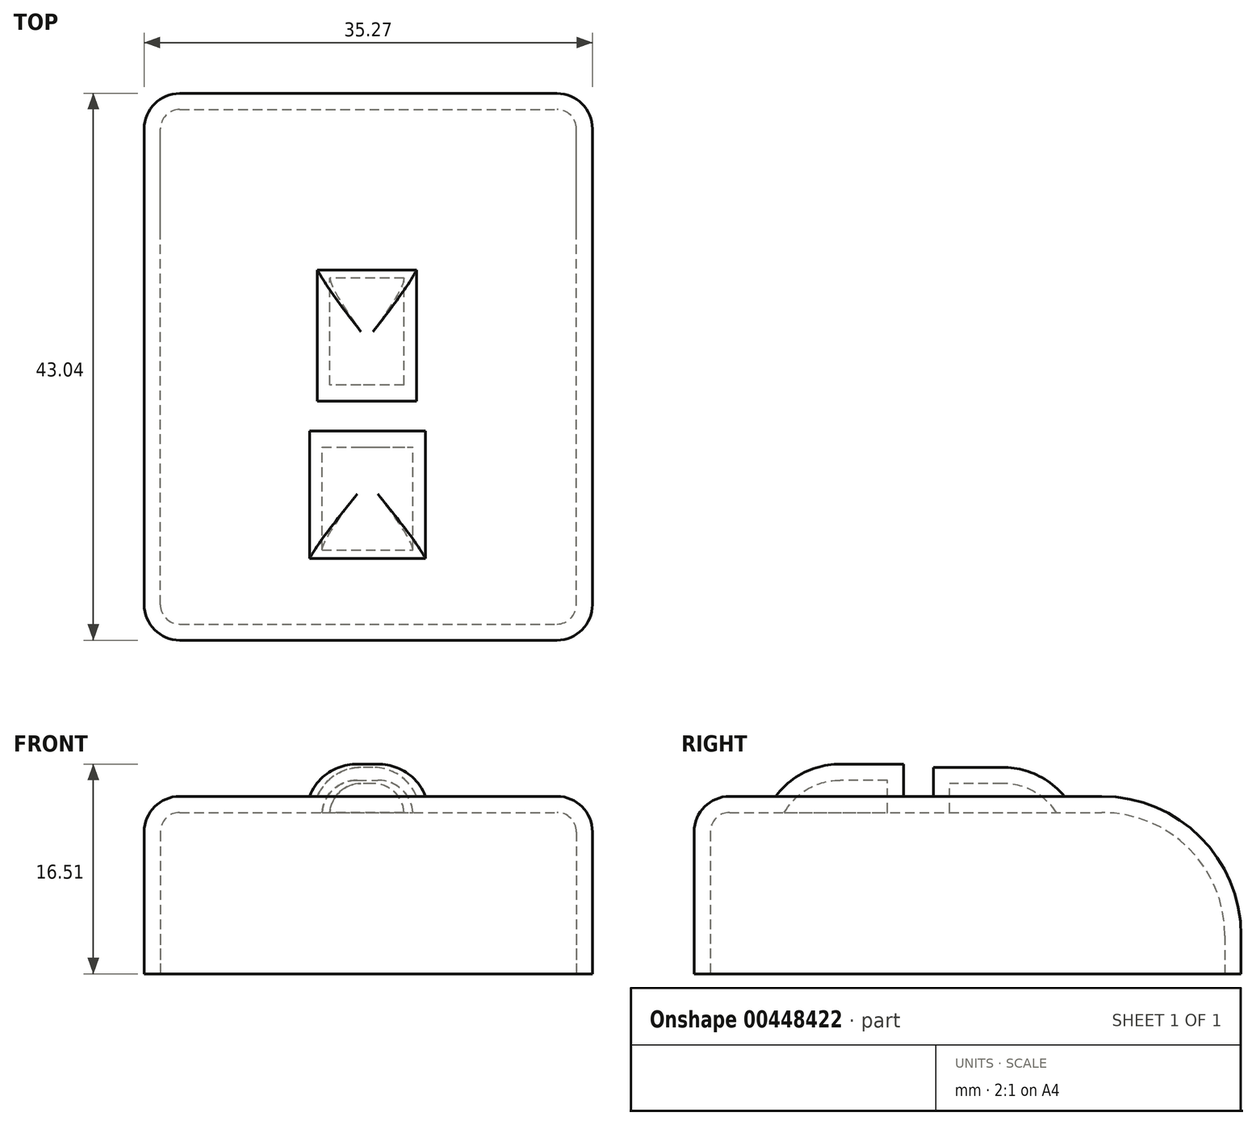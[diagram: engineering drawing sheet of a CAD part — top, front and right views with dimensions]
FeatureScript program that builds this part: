
annotation { "Feature Type Name" : "Feature", "Feature Type Description" : "" }
export const myFeature = defineFeature(function(context is Context, id is Id, definition is map)
    precondition{}
    {
        {
            var Q0;
            Q0=qCreatedBy(makeId("Top.planeOp"),FACE);
            var sketch = newSketch(context, id + "F0", { "sketchPlane" : qUnion([Q0])});
            skLineSegment(sketch, "E0.bottom", {"start": v(0, 0) * mm, "end": v(32.73, 0) * mm});
            skLineSegment(sketch, "E0.top", {"start": v(0, 40.5) * mm, "end": v(32.73, 40.5) * mm});
            skLineSegment(sketch, "E0.left", {"start": v(0, 0) * mm, "end": v(0, 40.5) * mm});
            skLineSegment(sketch, "E0.right", {"start": v(32.73, 0) * mm, "end": v(32.73, 40.5) * mm});
            skSolve(sketch);
        }
        {
            var Q0;
            Q0 = qSketchRegion(id + "F0", true);
            extrude(context, id + "F1", {"entities" : qUnion([Q0]), "depth" : 12.7 * mm});
        }
        {
            var Q0;
            Q0=makeQuery(id+"F1.opExtrude","CAP_EDGE",EDGE,{"disambiguationData":[OSD([sQuery(id+"F0.wireOp",EDGE,"E0.left")])],"isStart":false});
            var Q1;
            Q1=makeQuery(id+"F1.opExtrude","SWEPT_EDGE",EDGE,{"disambiguationData":[OSD([sQuery(id+"F0.wireOp",EDGE,"E0.bottom"),sQuery(id+"F0.wireOp",EDGE,"E0.left")])]});
            var Q2;
            Q2=makeQuery(id+"F1.opExtrude","SWEPT_EDGE",EDGE,{"disambiguationData":[OSD([sQuery(id+"F0.wireOp",EDGE,"E0.top"),sQuery(id+"F0.wireOp",EDGE,"E0.left")])]});
            var Q3;
            Q3=makeQuery(id+"F1.opExtrude","SWEPT_EDGE",EDGE,{"disambiguationData":[OSD([sQuery(id+"F0.wireOp",EDGE,"E0.bottom"),sQuery(id+"F0.wireOp",EDGE,"E0.right")])]});
            var Q4;
            Q4=makeQuery(id+"F1.opExtrude","CAP_EDGE",EDGE,{"disambiguationData":[OSD([sQuery(id+"F0.wireOp",EDGE,"E0.right")])],"isStart":false});
            var Q5;
            Q5=makeQuery(id+"F1.opExtrude","CAP_EDGE",EDGE,{"disambiguationData":[OSD([sQuery(id+"F0.wireOp",EDGE,"E0.bottom")])],"isStart":false});
            var Q6;
            Q6=makeQuery(id+"F1.opExtrude","SWEPT_EDGE",EDGE,{"disambiguationData":[OSD([sQuery(id+"F0.wireOp",EDGE,"E0.top"),sQuery(id+"F0.wireOp",EDGE,"E0.right")])]});
            fillet(context, id + "F2", {"entities" : qUnion([Q0, Q1, Q2, Q3, Q4, Q5, Q6]), "radius" : 1.52 * mm, "tangentPropagation" : true, "allowEdgeOverflow" : false});
        }
        {
            var Q0;
            Q0=makeQuery(id+"F1.opExtrude","CAP_EDGE",EDGE,{"disambiguationData":[OSD([sQuery(id+"F0.wireOp",EDGE,"E0.top")])],"isStart":false});
            fillet(context, id + "F3", {"entities" : qUnion([Q0]), "radius" : 9.7 * mm, "tangentPropagation" : true, "allowEdgeOverflow" : false});
        }
        {
            var Q0;
            Q0=makeQuery(id+"F1.opExtrude","CAP_FACE",FACE,{"disambiguationData":[OSD([sQuery(id+"F0.wireOp",EDGE,"E0.bottom"),sQuery(id+"F0.wireOp",EDGE,"E0.top"),sQuery(id+"F0.wireOp",EDGE,"E0.left"),sQuery(id+"F0.wireOp",EDGE,"E0.right")])],"isStart":false});
            var sketch = newSketch(context, id + "F4", { "sketchPlane" : qUnion([Q0])});
            skLineSegment(sketch, "E1.bottom", {"start": v(12.73, 5.83) * mm, "end": v(19.88, 5.83) * mm});
            skLineSegment(sketch, "E1.top", {"start": v(12.73, 13.93) * mm, "end": v(19.88, 13.93) * mm});
            skLineSegment(sketch, "E1.left", {"start": v(12.73, 5.83) * mm, "end": v(12.73, 13.93) * mm});
            skLineSegment(sketch, "E1.right", {"start": v(19.88, 5.83) * mm, "end": v(19.88, 13.93) * mm});
            skSolve(sketch);
        }
        {
            var Q0;
            Q0 = qSketchRegion(id + "F4", true);
            extrude(context, id + "F5", {"entities" : qUnion([Q0]), "operationType" : NewBodyOperationType.ADD, "depth" : 2.54 * mm});
        }
        {
            var Q0;
            Q0=makeQuery(id+"F5.opExtrude","CAP_EDGE",EDGE,{"disambiguationData":[OSD([sQuery(id+"F4.wireOp",EDGE,"E1.bottom")])],"isStart":false});
            fillet(context, id + "F6", {"entities" : qUnion([Q0]), "radius" : 5.08 * mm, "tangentPropagation" : true, "allowEdgeOverflow" : false});
        }
        {
            var Q0;
            Q0=makeQuery(id+"F5.opExtrude","CAP_EDGE",EDGE,{"disambiguationData":[OSD([sQuery(id+"F4.wireOp",EDGE,"E1.left")])],"isStart":false});
            var Q1;
            Q1=makeQuery(id+"F5.opExtrude","CAP_EDGE",EDGE,{"disambiguationData":[OSD([sQuery(id+"F4.wireOp",EDGE,"E1.right")])],"isStart":false});
            fillet(context, id + "F7", {"entities" : qUnion([Q0, Q1]), "radius" : 2.76 * mm, "tangentPropagation" : true, "allowEdgeOverflow" : false});
        }
        {
            var Q0;
            Q0=makeQuery(id+"F1.opExtrude","CAP_FACE",FACE,{"disambiguationData":[OSD([sQuery(id+"F0.wireOp",EDGE,"E0.bottom"),sQuery(id+"F0.wireOp",EDGE,"E0.top"),sQuery(id+"F0.wireOp",EDGE,"E0.left"),sQuery(id+"F0.wireOp",EDGE,"E0.right")])],"isStart":false});
            var sketch = newSketch(context, id + "F8", { "sketchPlane" : qUnion([Q0])});
            skLineSegment(sketch, "E2.bottom", {"start": v(19.18, 18.82) * mm, "end": v(13.35, 18.82) * mm});
            skLineSegment(sketch, "E2.top", {"start": v(19.18, 27.23) * mm, "end": v(13.35, 27.23) * mm});
            skLineSegment(sketch, "E2.left", {"start": v(19.18, 18.82) * mm, "end": v(19.18, 27.23) * mm});
            skLineSegment(sketch, "E2.right", {"start": v(13.35, 18.82) * mm, "end": v(13.35, 27.23) * mm});
            skSolve(sketch);
        }
        {
            var Q0;
            Q0 = qSketchRegion(id + "F8", true);
            extrude(context, id + "F9", {"entities" : qUnion([Q0]), "operationType" : NewBodyOperationType.ADD, "depth" : 2.3 * mm});
        }
        {
            var Q0;
            Q0=makeQuery(id+"F9.opExtrude","CAP_EDGE",EDGE,{"disambiguationData":[OSD([sQuery(id+"F8.wireOp",EDGE,"E2.top")])],"isStart":false});
            fillet(context, id + "F10", {"entities" : qUnion([Q0]), "radius" : 5.08 * mm, "tangentPropagation" : true, "allowEdgeOverflow" : false});
        }
        {
            var Q0;
            Q0=makeQuery(id+"F9.opExtrude","CAP_EDGE",EDGE,{"disambiguationData":[OSD([sQuery(id+"F8.wireOp",EDGE,"E2.left")])],"isStart":false});
            var Q1;
            Q1=makeQuery(id+"F9.opExtrude","CAP_EDGE",EDGE,{"disambiguationData":[OSD([sQuery(id+"F8.wireOp",EDGE,"E2.right")])],"isStart":false});
            fillet(context, id + "F11", {"entities" : qUnion([Q0, Q1]), "radius" : 2.45 * mm, "tangentPropagation" : true, "allowEdgeOverflow" : false});
        }
        {
            var Q0;
            Q0=makeQuery(id+"F1.opExtrude","CAP_FACE",FACE,{"disambiguationData":[OSD([sQuery(id+"F0.wireOp",EDGE,"E0.bottom"),sQuery(id+"F0.wireOp",EDGE,"E0.top"),sQuery(id+"F0.wireOp",EDGE,"E0.left"),sQuery(id+"F0.wireOp",EDGE,"E0.right")])],"isStart":true});
            var Q1;
            Q1=makeQuery(id+"F1.opExtrude","SWEPT_BODY",BODY,{"disambiguationData":[OSD([sQuery(id+"F0.wireOp",EDGE,"E0.bottom"),sQuery(id+"F0.wireOp",EDGE,"E0.top"),sQuery(id+"F0.wireOp",EDGE,"E0.left"),sQuery(id+"F0.wireOp",EDGE,"E0.right")])]});
            shell(context, id + "F12", {"entities" : qUnion([Q0]), "parts" : qUnion([Q1]), "thickness" : 1.27 * mm, "oppositeDirection" : true});
        }
    });
